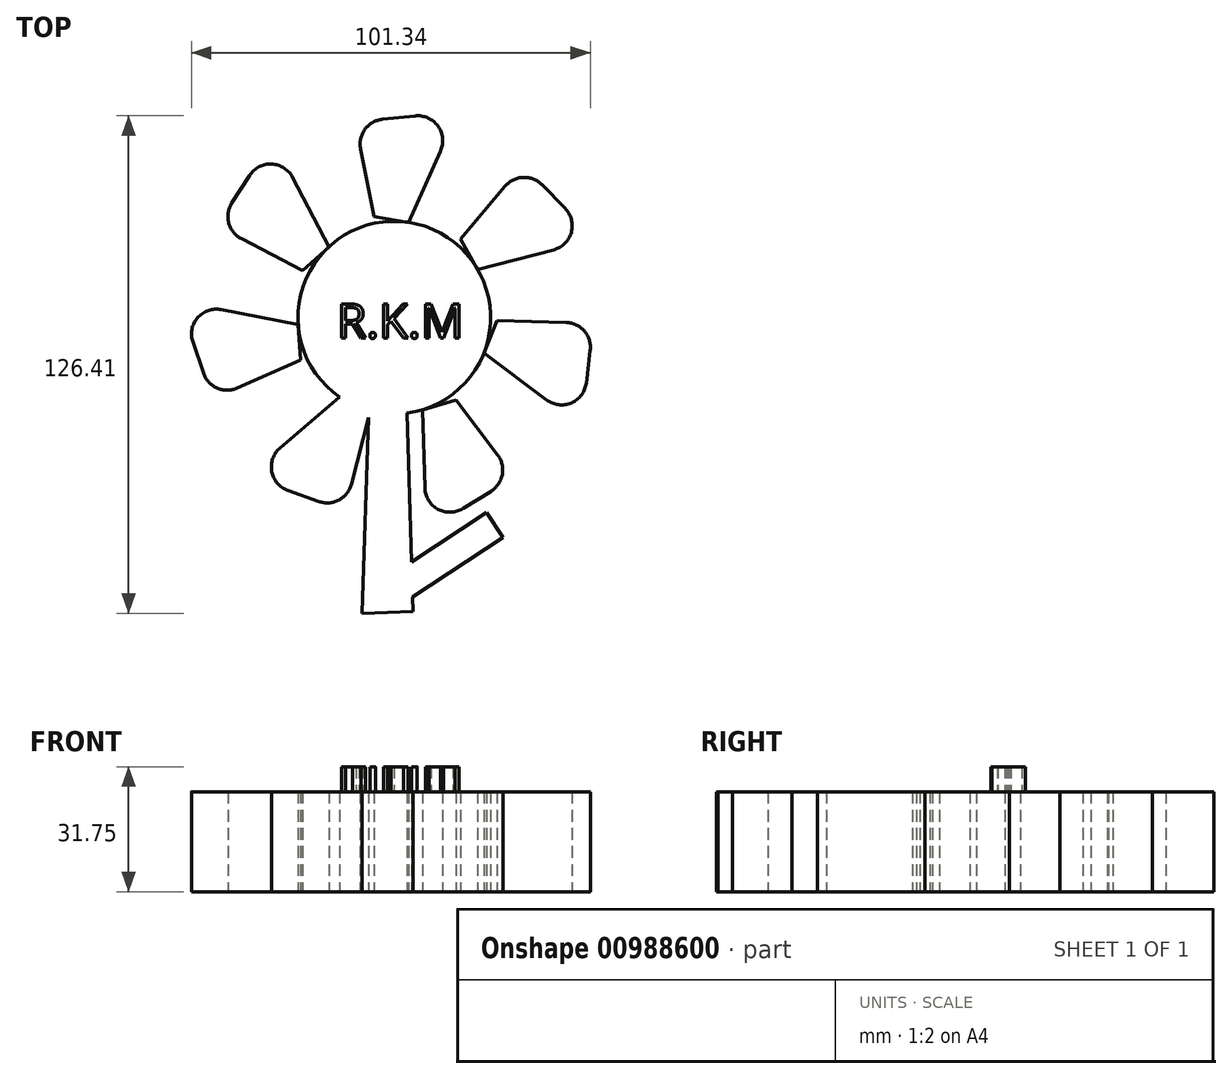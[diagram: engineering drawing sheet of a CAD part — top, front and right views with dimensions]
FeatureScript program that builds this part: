
annotation { "Feature Type Name" : "Feature", "Feature Type Description" : "" }
export const myFeature = defineFeature(function(context is Context, id is Id, definition is map)
    precondition{}
    {
        {
            var Q0;
            Q0=qCreatedBy(makeId("Top.planeOp"),FACE);
            var sketch = newSketch(context, id + "F0", { "sketchPlane" : qUnion([Q0])});
            skCircle(sketch, "E0", {"center": v(0, 0) * mm, "radius": 24.48 * mm});
            skLineSegment(sketch, "E1", {"start": v(21.23, 12.2) * mm, "end": v(40.46, 17.23) * mm});
            skLineSegment(sketch, "E2", {"start": v(43.38, 27.83) * mm, "end": v(37.55, 33.75) * mm});
            skLineSegment(sketch, "E3", {"start": v(28.17, 33.4) * mm, "end": v(16.84, 20) * mm});
            skLineSegment(sketch, "E4", {"start": v(16.84, 20) * mm, "end": v(21.23, 12.2) * mm});
            skPoint(sketch, "E5.visualSharp", {"position": v(32.67, 38.7) * mm});
            skArc(sketch, "E5.filletArc", {"start": v(37.55, 33.75) * mm, "mid": v(32.78, 35.64) * mm, "end": v(28.17, 33.4) * mm});
            skPoint(sketch, "E6.visualSharp", {"position": v(51.09, 20) * mm});
            skArc(sketch, "E6.filletArc", {"start": v(40.46, 17.23) * mm, "mid": v(44.98, 21.68) * mm, "end": v(43.38, 27.83) * mm});
            skLineSegment(sketch, "E7.1.0", {"start": v(-8.55, 42.85) * mm, "end": v(-5.14, 25.63) * mm});
            skArc(sketch, "E7.1.1", {"start": v(-2.98, 50.4) * mm, "mid": v(-7.43, 47.85) * mm, "end": v(-8.55, 42.85) * mm});
            skLineSegment(sketch, "E7.1.2", {"start": v(5.3, 51.27) * mm, "end": v(-2.98, 50.4) * mm});
            skArc(sketch, "E7.1.3", {"start": v(11.76, 42.38) * mm, "mid": v(11.1, 48.69) * mm, "end": v(5.3, 51.27) * mm});
            skLineSegment(sketch, "E7.1.4", {"start": v(3.7, 24.2) * mm, "end": v(11.76, 42.38) * mm});
            skLineSegment(sketch, "E7.1.5", {"start": v(-5.14, 25.63) * mm, "end": v(3.7, 24.2) * mm});
            skLineSegment(sketch, "E7.2.0", {"start": v(-38.83, 20.03) * mm, "end": v(-23.25, 11.96) * mm});
            skArc(sketch, "E7.2.1", {"start": v(-41.26, 29.1) * mm, "mid": v(-42.05, 24.03) * mm, "end": v(-38.83, 20.03) * mm});
            skLineSegment(sketch, "E7.2.2", {"start": v(-36.78, 36.1) * mm, "end": v(-41.26, 29.1) * mm});
            skArc(sketch, "E7.2.3", {"start": v(-25.8, 35.62) * mm, "mid": v(-31.15, 39.03) * mm, "end": v(-36.78, 36.1) * mm});
            skLineSegment(sketch, "E7.2.4", {"start": v(-16.62, 17.98) * mm, "end": v(-25.8, 35.62) * mm});
            skLineSegment(sketch, "E7.2.5", {"start": v(-23.25, 11.96) * mm, "end": v(-16.62, 17.98) * mm});
            skLineSegment(sketch, "E7.3.0", {"start": v(-39.88, -17.87) * mm, "end": v(-23.85, -10.72) * mm});
            skArc(sketch, "E7.3.1", {"start": v(-48.47, -14.12) * mm, "mid": v(-45, -17.9) * mm, "end": v(-39.88, -17.87) * mm});
            skLineSegment(sketch, "E7.3.2", {"start": v(-51.16, -6.25) * mm, "end": v(-48.47, -14.12) * mm});
            skArc(sketch, "E7.3.3", {"start": v(-43.93, 2.04) * mm, "mid": v(-49.93, -0.02) * mm, "end": v(-51.16, -6.25) * mm});
            skLineSegment(sketch, "E7.3.4", {"start": v(-24.42, -1.78) * mm, "end": v(-43.93, 2.04) * mm});
            skLineSegment(sketch, "E7.3.5", {"start": v(-23.85, -10.72) * mm, "end": v(-24.42, -1.78) * mm});
            skLineSegment(sketch, "E7.4.0", {"start": v(-10.9, -42.32) * mm, "end": v(-6.5, -25.33) * mm});
            skArc(sketch, "E7.4.1", {"start": v(-19.18, -46.7) * mm, "mid": v(-14.07, -46.34) * mm, "end": v(-10.9, -42.32) * mm});
            skLineSegment(sketch, "E7.4.2", {"start": v(-27.01, -43.9) * mm, "end": v(-19.18, -46.7) * mm});
            skArc(sketch, "E7.4.3", {"start": v(-28.98, -33.08) * mm, "mid": v(-31.12, -39.05) * mm, "end": v(-27.01, -43.9) * mm});
            skLineSegment(sketch, "E7.4.4", {"start": v(-13.83, -20.2) * mm, "end": v(-28.98, -33.08) * mm});
            skLineSegment(sketch, "E7.4.5", {"start": v(-6.5, -25.33) * mm, "end": v(-13.83, -20.2) * mm});
            skLineSegment(sketch, "E7.5.0", {"start": v(26.3, -34.9) * mm, "end": v(15.75, -20.87) * mm});
            skArc(sketch, "E7.5.1", {"start": v(24.55, -44.12) * mm, "mid": v(27.46, -39.9) * mm, "end": v(26.3, -34.9) * mm});
            skLineSegment(sketch, "E7.5.2", {"start": v(17.47, -48.49) * mm, "end": v(24.55, -44.12) * mm});
            skArc(sketch, "E7.5.3", {"start": v(7.8, -43.28) * mm, "mid": v(11.13, -48.68) * mm, "end": v(17.47, -48.49) * mm});
            skLineSegment(sketch, "E7.5.4", {"start": v(7.17, -23.4) * mm, "end": v(7.8, -43.28) * mm});
            skLineSegment(sketch, "E7.5.5", {"start": v(15.75, -20.87) * mm, "end": v(7.17, -23.4) * mm});
            skLineSegment(sketch, "E7.6.0", {"start": v(43.68, -1.2) * mm, "end": v(26.14, -0.7) * mm});
            skArc(sketch, "E7.6.1", {"start": v(49.8, -8.3) * mm, "mid": v(48.3, -3.4) * mm, "end": v(43.68, -1.2) * mm});
            skLineSegment(sketch, "E7.6.2", {"start": v(48.8, -16.57) * mm, "end": v(49.8, -8.3) * mm});
            skArc(sketch, "E7.6.3", {"start": v(38.7, -20.9) * mm, "mid": v(45, -21.65) * mm, "end": v(48.8, -16.57) * mm});
            skLineSegment(sketch, "E7.6.4", {"start": v(22.77, -8.99) * mm, "end": v(38.7, -20.9) * mm});
            skLineSegment(sketch, "E7.6.5", {"start": v(26.14, -0.7) * mm, "end": v(22.77, -8.99) * mm});
            skLineSegment(sketch, "E8", {"start": v(3.23, -24.27) * mm, "end": v(4.8, -74.7) * mm});
            skLineSegment(sketch, "E9", {"start": v(4.8, -74.7) * mm, "end": v(-8.19, -75.1) * mm});
            skLineSegment(sketch, "E10", {"start": v(-8.19, -75.1) * mm, "end": v(-6.5, -25.33) * mm});
            skLineSegment(sketch, "E11", {"start": v(4.4, -62.05) * mm, "end": v(23.46, -49.49) * mm});
            skPoint(sketch, "E11.endSnap0", {"position": v(4.01, -49.49) * mm});
            skLineSegment(sketch, "E12", {"start": v(23.46, -49.49) * mm, "end": v(27.66, -55.86) * mm});
            skLineSegment(sketch, "E13", {"start": v(27.66, -55.86) * mm, "end": v(4.69, -71.02) * mm});
            skSolve(sketch);
        }
        {
            var Q0;
            Q0=makeQuery(id+"F0.imprint","IMPRINT",FACE,{"disambiguationData":[TD([[makeQuery(id+"F0.imprint","IMPRINT",EDGE,{"derivedFrom":sQuery(id+"F0.wireOp",EDGE,"E1")}),1.0]])]});
            var Q1;
            Q1=makeQuery(id+"F0.imprint","IMPRINT",FACE,{"disambiguationData":[TD([[makeQuery(id+"F0.imprint","IMPRINT",EDGE,{"derivedFrom":sQuery(id+"F0.wireOp",EDGE,"E7.1.0")}),1.0]])]});
            var Q2;
            Q2=makeQuery(id+"F0.imprint","IMPRINT",FACE,{"disambiguationData":[TD([[makeQuery(id+"F0.imprint","IMPRINT",EDGE,{"derivedFrom":sQuery(id+"F0.wireOp",EDGE,"E7.2.0")}),1.0]])]});
            var Q3;
            Q3=makeQuery(id+"F0.imprint","IMPRINT",FACE,{"disambiguationData":[TD([[makeQuery(id+"F0.imprint","IMPRINT",EDGE,{"derivedFrom":sQuery(id+"F0.wireOp",EDGE,"E7.3.0")}),1.0]])]});
            var Q4;
            Q4=makeQuery(id+"F0.imprint","IMPRINT",FACE,{"disambiguationData":[TD([[makeQuery(id+"F0.imprint","IMPRINT",EDGE,{"derivedFrom":sQuery(id+"F0.wireOp",EDGE,"E7.5.0")}),1.0]])]});
            var Q5;
            Q5=makeQuery(id+"F0.imprint","IMPRINT",FACE,{"disambiguationData":[TD([[makeQuery(id+"F0.imprint","IMPRINT",EDGE,{"derivedFrom":sQuery(id+"F0.wireOp",EDGE,"E7.6.0")}),1.0]])]});
            var Q6;
            {var subQ0=sQuery(id+"F0.wireOp",EDGE,"E0");var subQ6=makeQuery(id+"F0.imprint","INTERSECT",VERTEX,{"derivedFrom":[subQ0,sQuery(id+"F0.wireOp",EDGE,"E8")]});Q6=makeQuery(id+"F0.imprint","IMPRINT",FACE,{"disambiguationData":[TD([[makeQuery(id+"F0.imprint","IMPRINT",EDGE,{"disambiguationData":[TD([[subQ6,1.0]])],"derivedFrom":subQ0}),1.0]])]});}
            var Q7;
            Q7=makeQuery(id+"F0.imprint","IMPRINT",FACE,{"disambiguationData":[TD([[makeQuery(id+"F0.imprint","IMPRINT",EDGE,{"derivedFrom":sQuery(id+"F0.wireOp",EDGE,"E7.4.0")}),1.0]])]});
            var Q8;
            {var subQ5=sQuery(id+"F0.wireOp",EDGE,"E7.4.5");Q8=makeQuery(id+"F0.imprint","IMPRINT",FACE,{"disambiguationData":[TD([[makeQuery(id+"F0.imprint","IMPRINT",EDGE,{"derivedFrom":subQ5}),-1.0]])]});}
            var Q9;
            {var subQ0=sQuery(id+"F0.wireOp",EDGE,"E11");Q9=makeQuery(id+"F0.imprint","IMPRINT",FACE,{"disambiguationData":[TD([[makeQuery(id+"F0.imprint","IMPRINT",EDGE,{"derivedFrom":subQ0}),-1.0]])]});}
            extrude(context, id + "F1", {"entities" : qUnion([Q0, Q1, Q2, Q3, Q4, Q5, Q6, Q7, Q8, Q9]), "depth" : 25.4 * mm, "offsetDistance" : 25.4 * mm});
        }
        {
            var Q0;
            Q0=makeQuery(id+"F1.opExtrude","CAP_FACE",FACE,{"disambiguationData":[OSD([sQuery(id+"F0.wireOp",EDGE,"E0"),sQuery(id+"F0.wireOp",EDGE,"E7.4.0"),sQuery(id+"F0.wireOp",EDGE,"E7.4.1"),sQuery(id+"F0.wireOp",EDGE,"E7.4.2"),sQuery(id+"F0.wireOp",EDGE,"E7.4.3"),sQuery(id+"F0.wireOp",EDGE,"E7.4.4"),sQuery(id+"F0.wireOp",EDGE,"E8"),sQuery(id+"F0.wireOp",EDGE,"E9"),sQuery(id+"F0.wireOp",EDGE,"E10"),sQuery(id+"F0.wireOp",EDGE,"E11"),sQuery(id+"F0.wireOp",EDGE,"E12"),sQuery(id+"F0.wireOp",EDGE,"E13")])],"isStart":false});
            var sketch = newSketch(context, id + "F2", { "sketchPlane" : qUnion([Q0])});
            skText(sketch, "E14", { "text": "R.K.M\n", "fontName": "OpenSans-Regular.ttf"});
            const initialGuessF2  = {"E14": [-0.01454, -0.00515, 1, 0, 0.00868]};
            skSetInitialGuess(sketch, initialGuessF2);
            skSolve(sketch);
        }
        {
            var Q0;
            Q0 = qSketchRegion(id + "F2", true);
            extrude(context, id + "F3", {"entities" : qUnion([Q0]), "operationType" : NewBodyOperationType.ADD, "depth" : 6.35 * mm, "offsetDistance" : 25.4 * mm});
        }
    });
